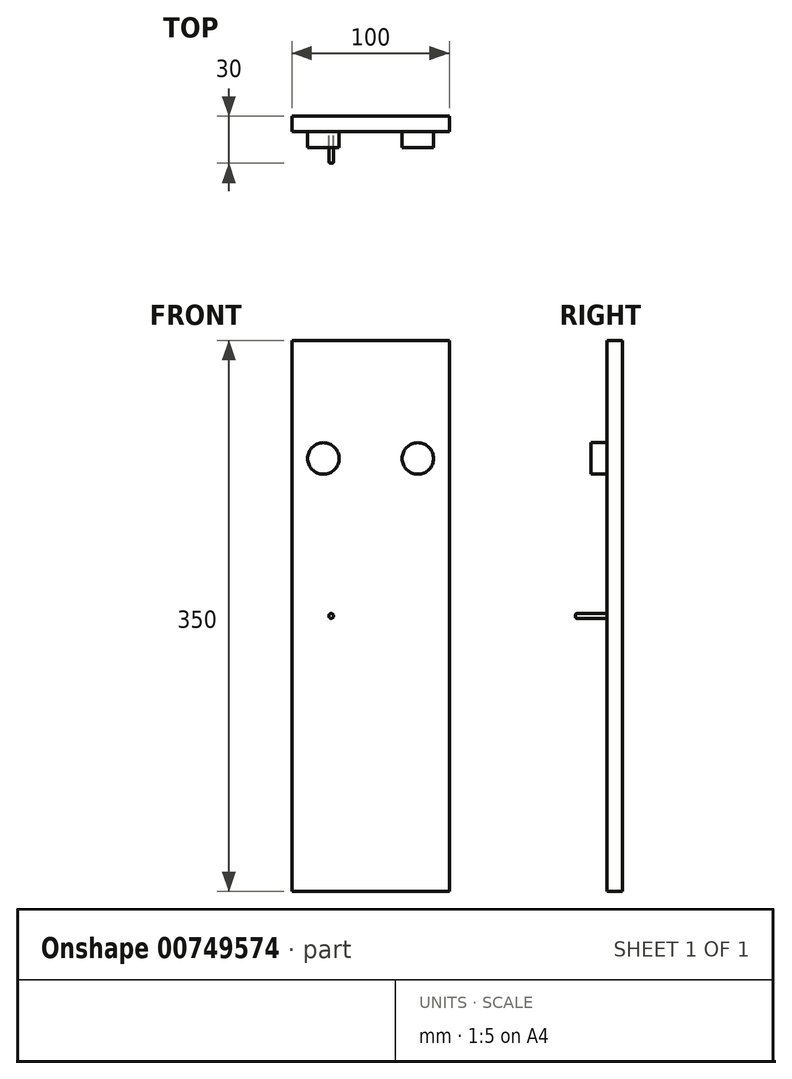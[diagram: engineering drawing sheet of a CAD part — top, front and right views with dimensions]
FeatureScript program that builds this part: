
annotation { "Feature Type Name" : "Feature", "Feature Type Description" : "" }
export const myFeature = defineFeature(function(context is Context, id is Id, definition is map)
    precondition{}
    {
        {
            var Q0;
            Q0=qCreatedBy(makeId("Front.planeOp"),FACE);
            var sketch = newSketch(context, id + "F0", { "sketchPlane" : qUnion([Q0])});
            skPoint(sketch, "E0.middle", {"position": v(0, 0) * mm});
            skCircle(sketch, "E1", {"center": v(-30, 0) * mm, "radius": 10 * mm});
            skCircle(sketch, "E2", {"center": v(30, 0) * mm, "radius": 10 * mm});
            skLineSegment(sketch, "E3.bottom", {"start": v(-50, 75) * mm, "end": v(50, 75) * mm});
            skLineSegment(sketch, "E3.top", {"start": v(-50, -275) * mm, "end": v(50, -275) * mm});
            skLineSegment(sketch, "E3.left", {"start": v(-50, 75) * mm, "end": v(-50, -275) * mm});
            skLineSegment(sketch, "E3.right", {"start": v(50, 75) * mm, "end": v(50, -275) * mm});
            skLineSegment(sketch, "E4.0", {"start": v(-30, 0) * mm, "end": v(-30, 0) * mm});
            skLineSegment(sketch, "E5", {"start": v(-30, 0) * mm, "end": v(30, 0) * mm, "construction": true});
            skSolve(sketch);
        }
        {
            var Q0;
            Q0=makeQuery(id+"F0.imprint","IMPRINT",FACE,{"disambiguationData":[TD([[makeQuery(id+"F0.imprint","IMPRINT",EDGE,{"derivedFrom":sQuery(id+"F0.wireOp",EDGE,"E1")}),-1.0]])]});
            extrude(context, id + "F1", {"entities" : qUnion([Q0]), "depth" : 10 * mm, "offsetDistance" : 25 * mm});
        }
        {
            var Q0;
            Q0=makeQuery(id+"F0.imprint","IMPRINT",FACE,{"disambiguationData":[TD([[makeQuery(id+"F0.imprint","IMPRINT",EDGE,{"derivedFrom":sQuery(id+"F0.wireOp",EDGE,"E1")}),1.0]])]});
            var Q1;
            Q1=makeQuery(id+"F0.imprint","IMPRINT",FACE,{"disambiguationData":[TD([[makeQuery(id+"F0.imprint","IMPRINT",EDGE,{"derivedFrom":sQuery(id+"F0.wireOp",EDGE,"E2")}),1.0]])]});
            extrude(context, id + "F2", {"entities" : qUnion([Q0, Q1]), "operationType" : NewBodyOperationType.ADD, "depth" : 20 * mm, "offsetDistance" : 25 * mm});
        }
        {
            var Q0;
            Q0=makeQuery(id+"F1.opExtrude","CAP_FACE",FACE,{"disambiguationData":[OSD([sQuery(id+"F0.wireOp",EDGE,"E1"),sQuery(id+"F0.wireOp",EDGE,"E2"),sQuery(id+"F0.wireOp",EDGE,"E3.bottom"),sQuery(id+"F0.wireOp",EDGE,"E3.top"),sQuery(id+"F0.wireOp",EDGE,"E3.left"),sQuery(id+"F0.wireOp",EDGE,"E3.right")])],"isStart":false});
            var sketch = newSketch(context, id + "F3", { "sketchPlane" : qUnion([Q0])});
            skCircle(sketch, "E6", {"center": v(-25, -100) * mm, "radius": 1.5 * mm});
            skPoint(sketch, "E7", {"position": v(-30, 0) * mm});
            skSolve(sketch);
        }
        {
            var Q0;
            Q0=makeQuery(id+"F3.imprint","IMPRINT",FACE,{"disambiguationData":[TD([[makeQuery(id+"F3.imprint","IMPRINT",EDGE,{"derivedFrom":sQuery(id+"F3.wireOp",EDGE,"E6")}),1.0]])]});
            extrude(context, id + "F4", {"entities" : qUnion([Q0]), "operationType" : NewBodyOperationType.ADD, "depth" : 20 * mm, "offsetDistance" : 25 * mm});
        }
        {
            var Q0;
            Q0=makeQuery(id+"F4.opExtrude","CAP_EDGE",EDGE,{"disambiguationData":[OSD([sQuery(id+"F3.wireOp",EDGE,"E6")])],"isStart":false});
            fillet(context, id + "F5", {"entities" : qUnion([Q0]), "radius" : 1 * mm, "tangentPropagation" : true, "allowEdgeOverflow" : false});
        }
    });
